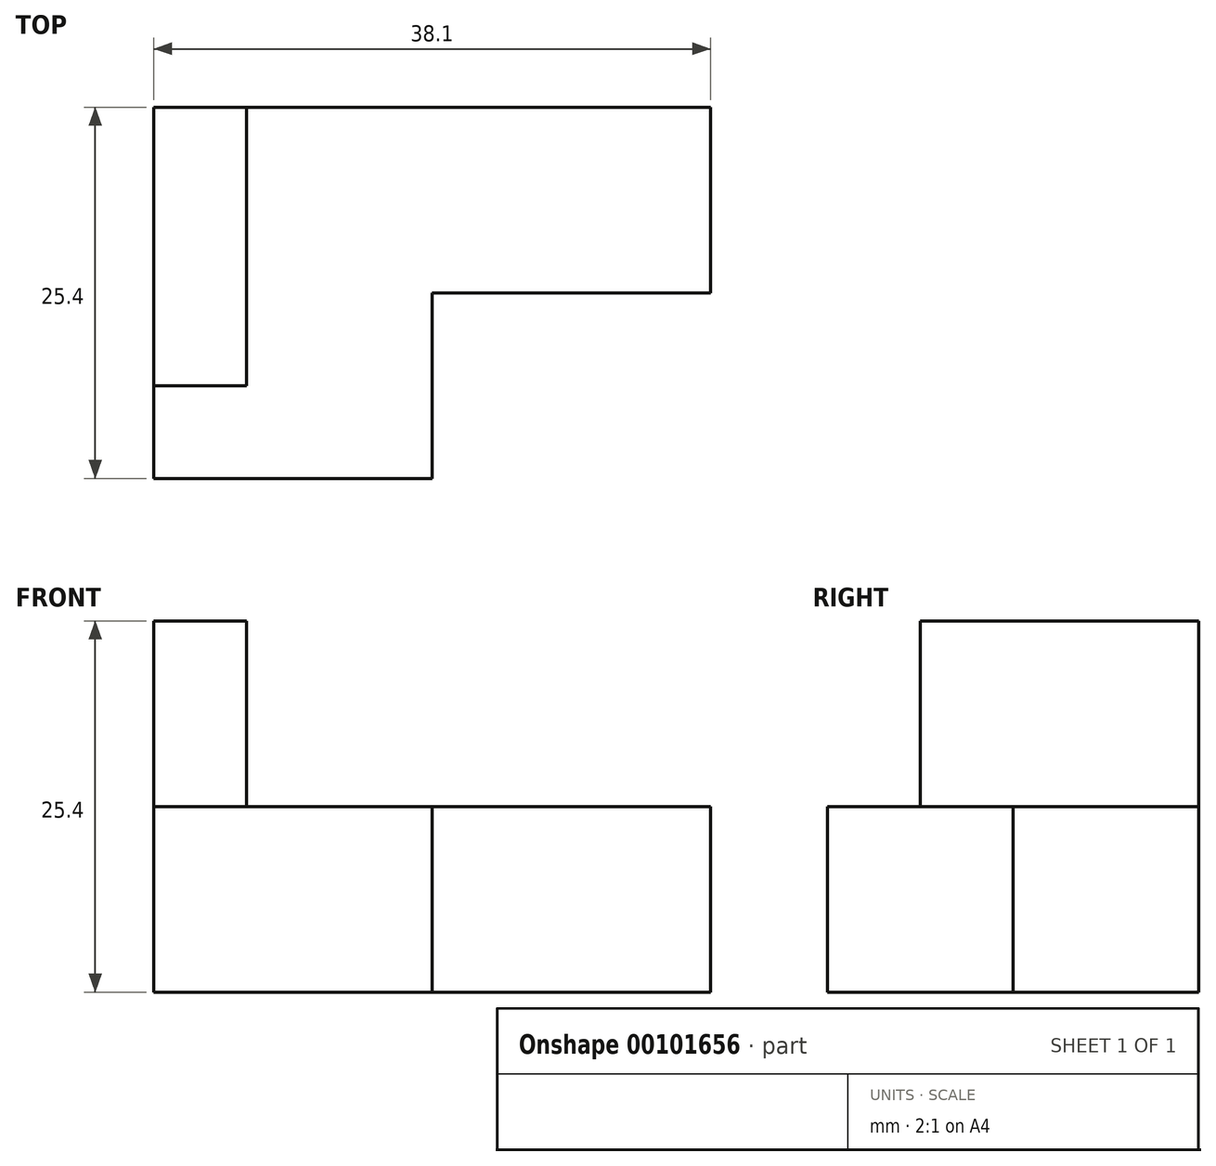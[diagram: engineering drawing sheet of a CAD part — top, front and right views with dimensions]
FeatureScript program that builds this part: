
annotation { "Feature Type Name" : "Feature", "Feature Type Description" : "" }
export const myFeature = defineFeature(function(context is Context, id is Id, definition is map)
    precondition{}
    {
        {
            var Q0;
            Q0=qCreatedBy(makeId("Front.planeOp"),FACE);
            var sketch = newSketch(context, id + "F0", { "sketchPlane" : qUnion([Q0])});
            skLineSegment(sketch, "E0", {"start": v(0, 0) * mm, "end": v(0, 12.7) * mm});
            skLineSegment(sketch, "E1", {"start": v(0, 12.7) * mm, "end": v(19.05, 12.7) * mm});
            skLineSegment(sketch, "E2", {"start": v(19.05, 12.7) * mm, "end": v(19.05, 0) * mm});
            skLineSegment(sketch, "E3", {"start": v(19.05, 0) * mm, "end": v(0, 0) * mm});
            skLineSegment(sketch, "E4", {"start": v(19.05, 0) * mm, "end": v(38.1, 0) * mm});
            skLineSegment(sketch, "E5", {"start": v(38.1, 0) * mm, "end": v(38.1, 12.7) * mm});
            skLineSegment(sketch, "E6", {"start": v(38.1, 12.7) * mm, "end": v(19.05, 12.7) * mm});
            skLineSegment(sketch, "E7", {"start": v(0, 12.7) * mm, "end": v(0, 25.4) * mm});
            skLineSegment(sketch, "E8", {"start": v(0, 25.4) * mm, "end": v(6.35, 25.4) * mm});
            skLineSegment(sketch, "E9", {"start": v(6.35, 25.4) * mm, "end": v(6.35, 12.7) * mm});
            skSolve(sketch);
        }
        {
            var Q0;
            {var subQ3=sQuery(id+"F0.wireOp",EDGE,"E0");Q0=makeQuery(id+"F0.imprint","IMPRINT",FACE,{"disambiguationData":[TD([[makeQuery(id+"F0.imprint","IMPRINT",EDGE,{"derivedFrom":subQ3}),-1.0]])]});}
            extrude(context, id + "F1", {"entities" : qUnion([Q0]), "depth" : 25.4 * mm});
        }
        {
            var Q0;
            {var subQ0=sQuery(id+"F0.wireOp",EDGE,"E7");Q0=makeQuery(id+"F0.imprint","IMPRINT",FACE,{"disambiguationData":[TD([[makeQuery(id+"F0.imprint","IMPRINT",EDGE,{"derivedFrom":subQ0}),-1.0]])]});}
            extrude(context, id + "F2", {"entities" : qUnion([Q0]), "operationType" : NewBodyOperationType.ADD, "depth" : 19.05 * mm});
        }
        {
            var Q0;
            Q0=makeQuery(id+"F0.imprint","IMPRINT",FACE,{"disambiguationData":[TD([[makeQuery(id+"F0.imprint","IMPRINT",EDGE,{"derivedFrom":sQuery(id+"F0.wireOp",EDGE,"E2")}),1.0]])]});
            extrude(context, id + "F3", {"entities" : qUnion([Q0]), "operationType" : NewBodyOperationType.ADD, "depth" : 12.7 * mm});
        }
    });
